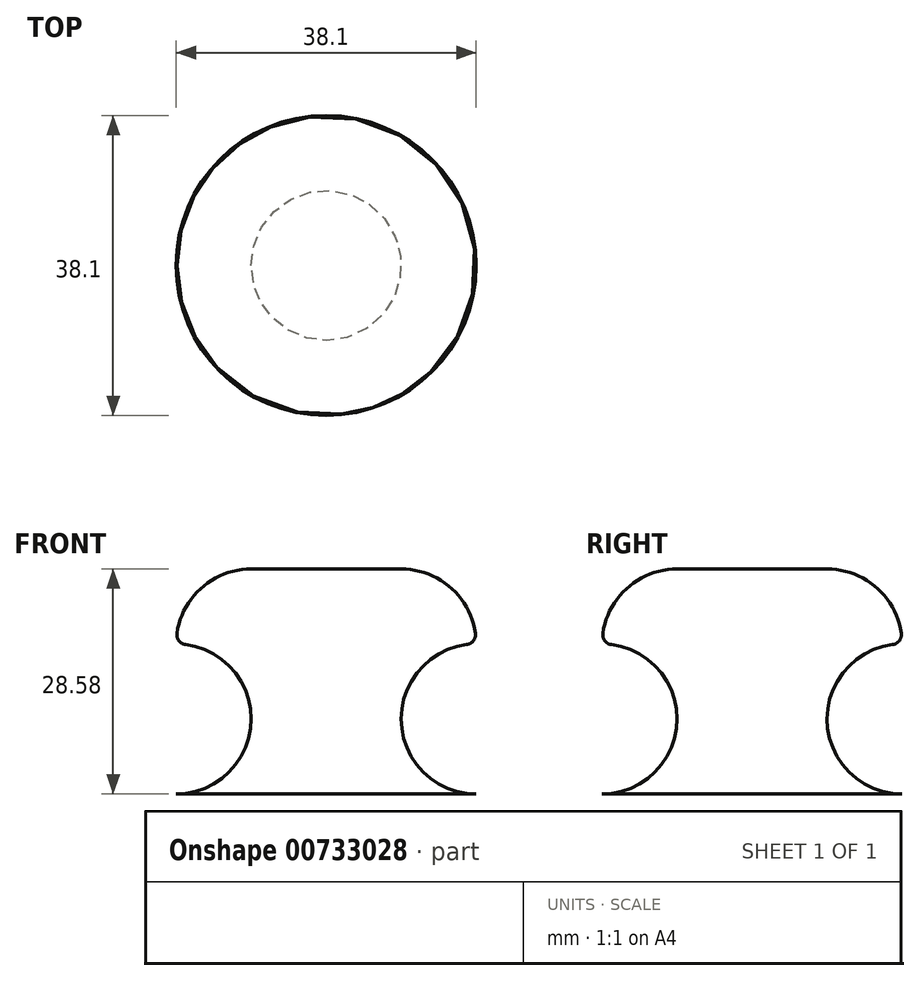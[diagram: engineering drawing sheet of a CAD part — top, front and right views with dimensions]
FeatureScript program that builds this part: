
annotation { "Feature Type Name" : "Feature", "Feature Type Description" : "" }
export const myFeature = defineFeature(function(context is Context, id is Id, definition is map)
    precondition{}
    {
        {
            var Q0;
            Q0=qCreatedBy(makeId("Front.planeOp"),FACE);
            var sketch = newSketch(context, id + "F0", { "sketchPlane" : qUnion([Q0])});
            skLineSegment(sketch, "E0", {"start": v(0, 0) * mm, "end": v(19.05, 0) * mm});
            skLineSegment(sketch, "E1", {"start": v(0, 0) * mm, "end": v(0, 28.58) * mm});
            skLineSegment(sketch, "E2", {"start": v(0, 28.58) * mm, "end": v(9.53, 28.58) * mm});
            skLineSegment(sketch, "E3", {"start": v(19.05, 19.05) * mm, "end": v(19.05, 19.05) * mm});
            skPoint(sketch, "E4", {"position": v(9.53, 9.53) * mm});
            skArc(sketch, "E5", {"start": v(19.05, 19.05) * mm, "mid": v(9.53, 9.53) * mm, "end": v(19.05, 0) * mm});
            skPoint(sketch, "E6.visualSharp", {"position": v(19.05, 28.58) * mm});
            skArc(sketch, "E6.filletArc", {"start": v(19.05, 19.05) * mm, "mid": v(16.26, 25.79) * mm, "end": v(9.53, 28.58) * mm});
            skSolve(sketch);
        }
        {
            var Q0;
            Q0=makeQuery(id+"F0.imprint","IMPRINT",FACE,{"disambiguationData":[TD([[makeQuery(id+"F0.imprint","IMPRINT",EDGE,{"derivedFrom":sQuery(id+"F0.wireOp",EDGE,"E0")}),1.0]])]});
            var Q1;
            Q1=sQuery(id+"F0.wireOp",EDGE,"E1");
            revolve(context, id + "F1", {"surfaceOperationType" : NewSurfaceOperationType.NEW, "entities" : qUnion([Q0]), "axis" : qUnion([Q1]), "revolveType" : RevolveType.FULL});
        }
        {
            var Q0;
            Q0=makeQuery(id+"F1.opRevolve","SWEPT_EDGE",EDGE,{"disambiguationData":[OSD([sQuery(id+"F0.wireOp",EDGE,"E5"),sQuery(id+"F0.wireOp",EDGE,"E6.filletArc")])]});
            fillet(context, id + "F2", {"entities" : qUnion([Q0]), "radius" : 1.27 * mm, "tangentPropagation" : true, "allowEdgeOverflow" : false});
        }
    });
